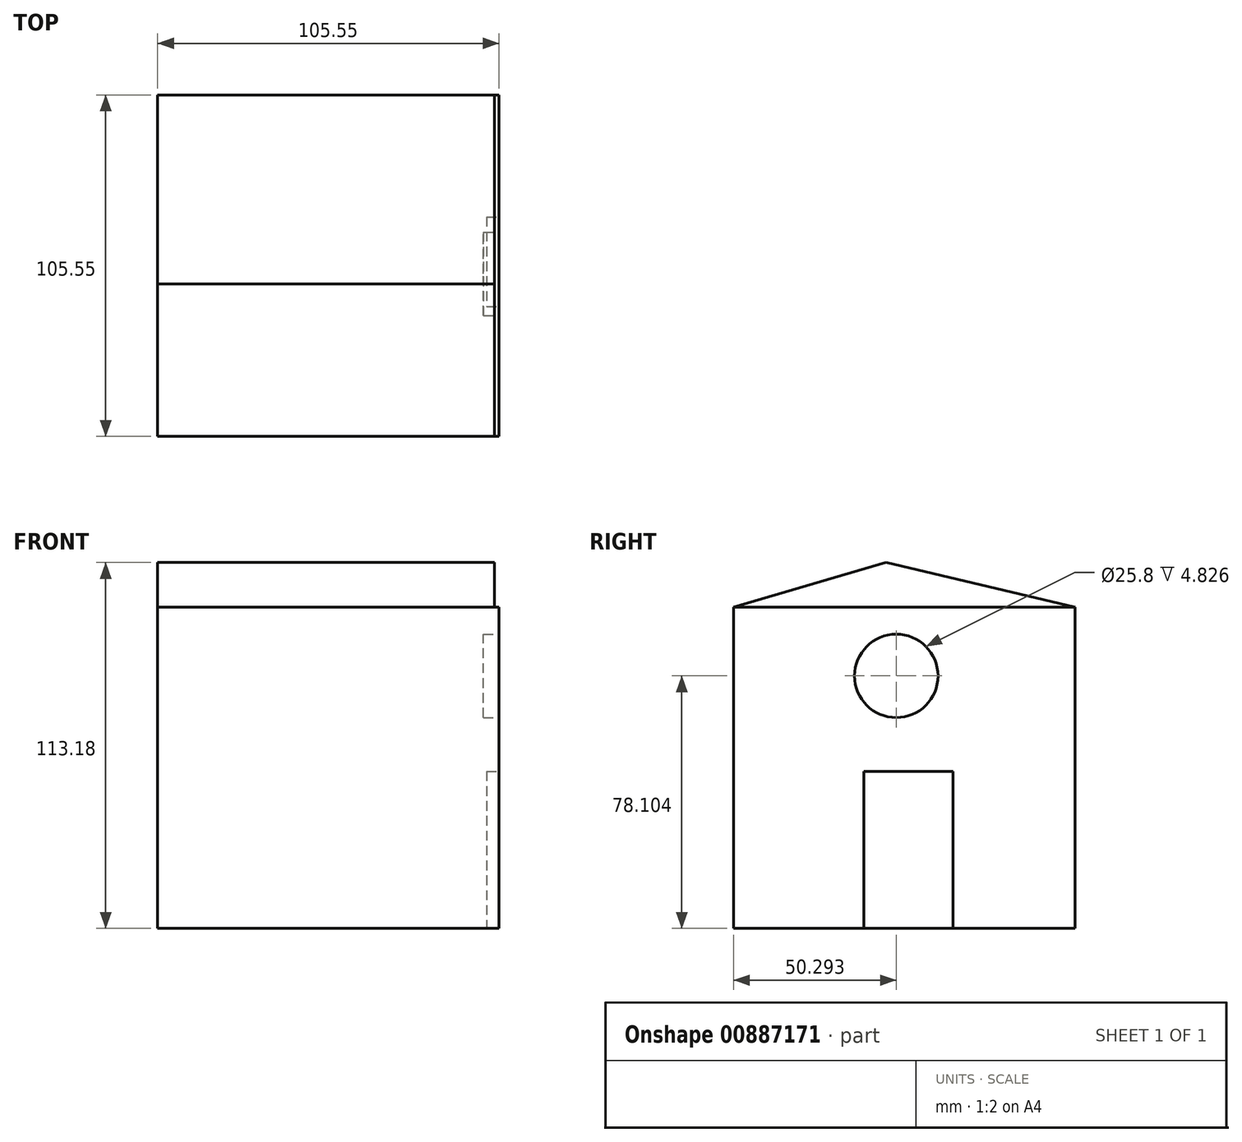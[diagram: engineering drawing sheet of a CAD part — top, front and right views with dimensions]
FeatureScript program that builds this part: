
annotation { "Feature Type Name" : "Feature", "Feature Type Description" : "" }
export const myFeature = defineFeature(function(context is Context, id is Id, definition is map)
    precondition{}
    {
        {
            var Q0;
            Q0=qCreatedBy(makeId("Top.planeOp"),FACE);
            var sketch = newSketch(context, id + "F0", { "sketchPlane" : qUnion([Q0])});
            skLineSegment(sketch, "E0.bottom", {"start": v(-51.9, 46.04) * mm, "end": v(53.65, 46.04) * mm});
            skLineSegment(sketch, "E0.top", {"start": v(-51.9, -59.51) * mm, "end": v(53.65, -59.51) * mm});
            skLineSegment(sketch, "E0.left", {"start": v(-51.9, 46.04) * mm, "end": v(-51.9, -59.51) * mm});
            skLineSegment(sketch, "E0.right", {"start": v(53.65, 46.04) * mm, "end": v(53.65, -59.51) * mm});
            skSolve(sketch);
        }
        {
            var Q0;
            Q0 = qSketchRegion(id + "F0", true);
            extrude(context, id + "F1", {"entities" : qUnion([Q0]), "depth" : 99.31 * mm, "offsetDistance" : 25.4 * mm});
        }
        {
            var Q0;
            Q0=makeQuery(id+"F1.opExtrude","SWEPT_FACE",FACE,{"disambiguationData":[OSD([sQuery(id+"F0.wireOp",EDGE,"E0.left")])]});
            var sketch = newSketch(context, id + "F2", { "sketchPlane" : qUnion([Q0])});
            skLineSegment(sketch, "E1", {"start": v(-46.04, 99.31) * mm, "end": v(12.35, 113.18) * mm});
            skLineSegment(sketch, "E2", {"start": v(12.35, 113.18) * mm, "end": v(59.51, 99.31) * mm});
            skLineSegment(sketch, "E3", {"start": v(59.51, 99.31) * mm, "end": v(-46.04, 99.31) * mm});
            skSolve(sketch);
        }
        {
            var Q0;
            Q0 = qSketchRegion(id + "F2", true);
            extrude(context, id + "F3", {"entities" : qUnion([Q0]), "operationType" : NewBodyOperationType.ADD, "oppositeDirection" : true, "depth" : 104.14 * mm, "offsetDistance" : 25.4 * mm});
        }
        {
            var Q0;
            Q0=makeQuery(id+"F1.opExtrude","SWEPT_FACE",FACE,{"disambiguationData":[OSD([sQuery(id+"F0.wireOp",EDGE,"E0.right")])]});
            var sketch = newSketch(context, id + "F4", { "sketchPlane" : qUnion([Q0])});
            skLineSegment(sketch, "E4.bottom", {"start": v(-19.3, 48.6) * mm, "end": v(8.38, 48.6) * mm});
            skLineSegment(sketch, "E4.top", {"start": v(-19.3, 0) * mm, "end": v(8.38, 0) * mm});
            skLineSegment(sketch, "E4.left", {"start": v(-19.3, 48.6) * mm, "end": v(-19.3, 0) * mm});
            skLineSegment(sketch, "E4.right", {"start": v(8.38, 48.6) * mm, "end": v(8.38, 0) * mm});
            skSolve(sketch);
        }
        {
            var Q0;
            Q0 = qSketchRegion(id + "F4", true);
            extrude(context, id + "F5", {"entities" : qUnion([Q0]), "operationType" : NewBodyOperationType.REMOVE, "oppositeDirection" : true, "depth" : 3.8 * mm, "offsetDistance" : 25.4 * mm});
        }
        {
            var Q0;
            Q0=makeQuery(id+"F1.opExtrude","SWEPT_FACE",FACE,{"disambiguationData":[OSD([sQuery(id+"F0.wireOp",EDGE,"E0.right")])]});
            var sketch = newSketch(context, id + "F6", { "sketchPlane" : qUnion([Q0])});
            skCircle(sketch, "E5", {"center": v(-9.22, 78.1) * mm, "radius": 12.9 * mm});
            skSolve(sketch);
        }
        {
            var Q0;
            Q0 = qSketchRegion(id + "F6", true);
            extrude(context, id + "F7", {"entities" : qUnion([Q0]), "operationType" : NewBodyOperationType.REMOVE, "oppositeDirection" : true, "depth" : 4.83 * mm, "offsetDistance" : 25.4 * mm});
        }
    });
